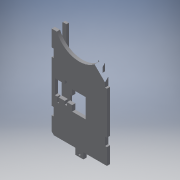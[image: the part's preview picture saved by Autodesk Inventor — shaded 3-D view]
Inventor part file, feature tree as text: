
AUTODESK INVENTOR PART (.ipt)
format: ipt  version: 2016 (Build 200138000, 138)  size: 296,960 bytes
history: native  units: in
note: dims shown in document units (in); Inventor stores cm internally (conversion verified against a paired STEP export)
features: reference x14, extrude x12, sketch x11, plane x1
ambient origin geometry x8: Origin, YZ Plane, XZ Plane, XY Plane, X Axis, Y Axis, Z Axis, Center Point
bodies: Solid1 (feature_tree)
feature tree (38):
  extrude  "Extrusion1"  Depth=0.1969in TaperAngle=0.0deg
  extrude  "Extrusion2"  Depth=0.1969in TaperAngle=0.0deg
  extrude  "Extrusion3"  Depth=0.0787in
  extrude  "Extrusion4"  Depth=0.1969in TaperAngle=0.0deg
  extrude  "Extrusion6"  Depth=0.1969in
  extrude  "Extrusion7"  Depth=0.1969in TaperAngle=0.0deg
  extrude  "Extrusion8"  Depth=0.5in
  plane  "Work Plane1"
  extrude  "Extrusion18"  Depth=0.25in TaperAngle=0.0deg
  extrude  "Extrusion19"  Depth=0.15in
  extrude  "Extrusion20"  Depth=0.0394in
  extrude  "Extrusion21"  Depth=1.0in TaperAngle=0.0deg
  extrude  "Extrusion22"  Depth=0.15in
  sketch  "Sketch1"  dims[d0=6.0in d1=0.1969in d2=0.0in]
  sketch  "Sketch2"  dims[d3=0.5906in d4=0.1969in d5=0.0in]
  reference  "Reference2"
  reference  "Reference3"
  sketch  "Sketch4"  dims[d6=3.0in d7=0.0787in]
  sketch  "Sketch6"  dims[d8=0.0787in d9=0.1969in d10=0.0in]
  sketch  "Sketch7"  dims[d11=0.1969in d12=0.1969in]
  sketch  "Sketch8"  dims[d13=0.1969in d14=0.1969in d15=0.0in]
  reference  "Reference6"
  reference  "Reference7"
  reference  "Reference8"
  reference  "Reference9"
  reference  "Reference10"
  reference  "Reference11"
  reference  "Reference12"
  reference  "Reference13"
  reference  "Reference14"
  reference  "Reference15"
  sketch  "Sketch18"  dims[d18=0.25in d19=0.5in]
  sketch  "Sketch20"  dims[d20=0.4in d21=0.0in d24=0.25in d25=0.0in]
  sketch  "Sketch21"  dims[d26=0.15in d27=0.1378in]
  reference  "Reference29"
  sketch  "Sketch22"  dims[d28=0.0394in d29=0.1181in]
  sketch  "Sketch23"  dims[d30=0.0394in d31=1.0in d32=0.0in d33=0.02in d34=0.325in d35=0.02in d45=0.0197in d46=0.0197in d47=0.0197in d73=0.1181in d83=1.0in d84=0.5in d85=0.118in d86=1.0in d87=0.5in d88=0.118in d89=0.3937in d90=0.0in d91=0.8226in d92=0.0in d93=0.2in d94=0.0in d95=0.1in d96=0.0in d97=0.15in d98=0.0in]
  reference  "Reference30"
